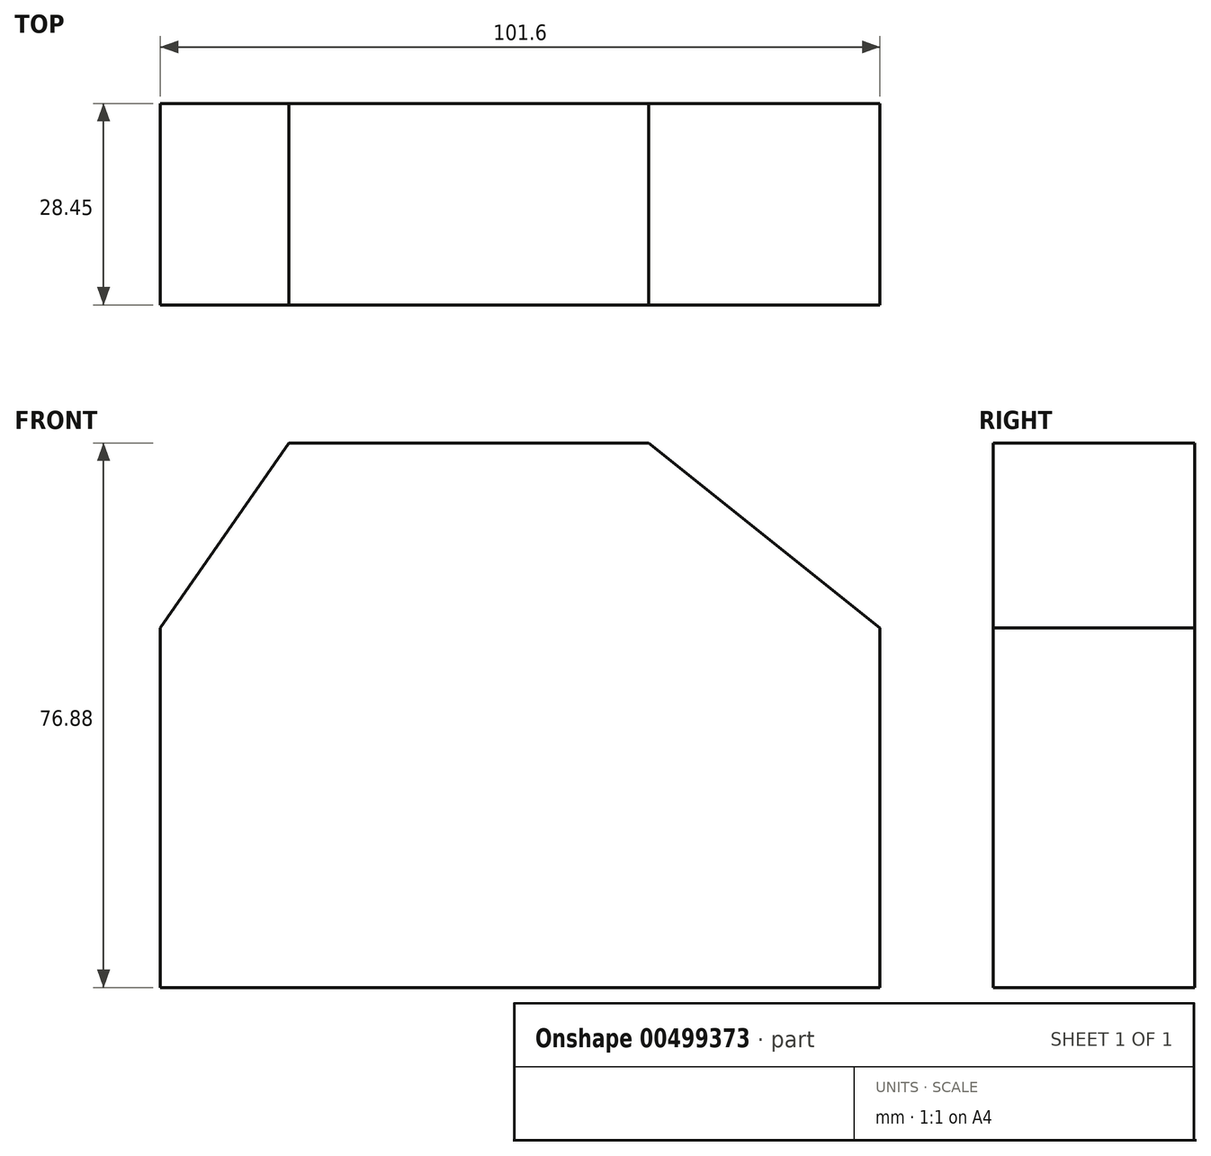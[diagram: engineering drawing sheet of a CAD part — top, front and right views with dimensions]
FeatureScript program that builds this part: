
annotation { "Feature Type Name" : "Feature", "Feature Type Description" : "" }
export const myFeature = defineFeature(function(context is Context, id is Id, definition is map)
    precondition{}
    {
        {
            var Q0;
            Q0=qCreatedBy(makeId("Front.planeOp"),FACE);
            var sketch = newSketch(context, id + "F0", { "sketchPlane" : qUnion([Q0])});
            skLineSegment(sketch, "E0", {"start": v(0, 0) * mm, "end": v(101.6, 0) * mm});
            skLineSegment(sketch, "E1", {"start": v(101.6, 0) * mm, "end": v(101.6, 50.8) * mm});
            skLineSegment(sketch, "E2", {"start": v(101.6, 50.8) * mm, "end": v(68.96, 76.88) * mm});
            skLineSegment(sketch, "E3", {"start": v(68.96, 76.88) * mm, "end": v(18.16, 76.88) * mm});
            skLineSegment(sketch, "E4", {"start": v(18.16, 76.88) * mm, "end": v(0, 50.8) * mm});
            skLineSegment(sketch, "E5", {"start": v(0, 50.8) * mm, "end": v(0, 0) * mm});
            skSolve(sketch);
        }
        {
            var Q0;
            Q0=makeQuery(id+"F0.imprint","IMPRINT",FACE,{"disambiguationData":[TD([[makeQuery(id+"F0.imprint","IMPRINT",EDGE,{"derivedFrom":sQuery(id+"F0.wireOp",EDGE,"E0")}),1.0]])]});
            extrude(context, id + "F1", {"entities" : qUnion([Q0]), "depth" : 28.45 * mm});
        }
    });
